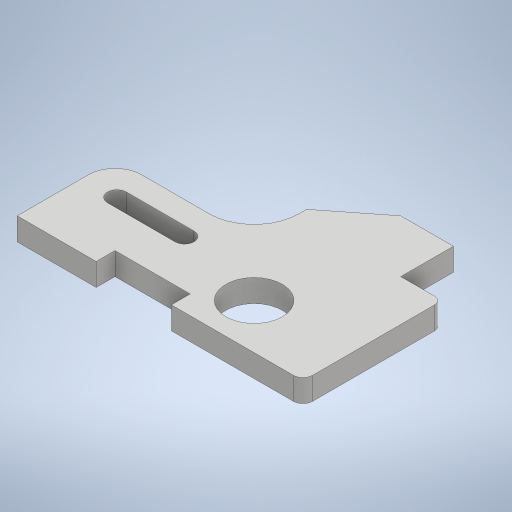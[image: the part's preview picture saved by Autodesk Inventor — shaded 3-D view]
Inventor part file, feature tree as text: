
AUTODESK INVENTOR PART (.ipt)
format: ipt  version: 2024 (Build 280153000, 153)  size: 263,680 bytes
history: native  units: mm
features: sketch x2, extrude x1
ambient origin geometry x8: Origin, YZ Plane, XZ Plane, XY Plane, X Axis, Y Axis, Z Axis, Center Point
bodies: Solid1 (feature_tree)
feature tree (3):
  sketch  "Sketch1"  dims[d0=52.0mm d5=74.0mm d7=102.0mm d8=80.0mm d9=102.0mm d11=42.0mm d12=82.0mm d13=152.0mm d14=74.0mm d15=14.0mm d16=24.0mm d17=4.0mm d18=5.0mm d30=30.0mm d31=24.0mm d32=102.0mm d33=10.0mm d34=23.008815mm d35=24.215931mm d38=130.0mm d42=5.0mm d43=18.0mm d44=54.0mm d45=35.0mm d46=5.0mm d47=12.0mm d48=0.0mm]
  sketch  "3D Sketch1"
  extrude  "Extrusion1"  Depth=74.0mm
